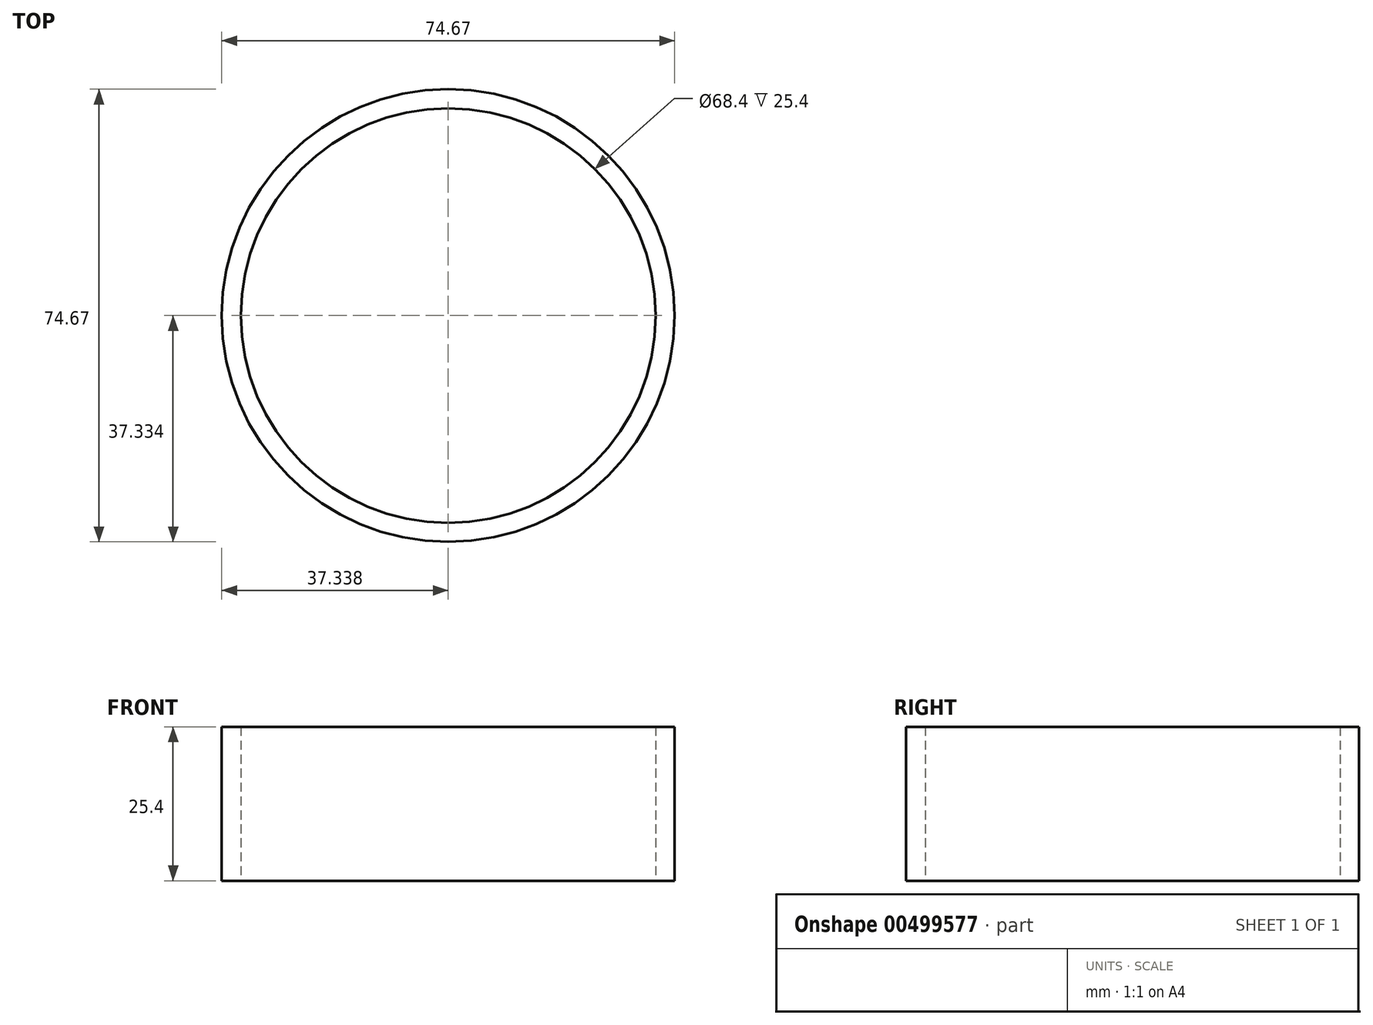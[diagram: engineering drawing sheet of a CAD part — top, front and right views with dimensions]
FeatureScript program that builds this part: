
annotation { "Feature Type Name" : "Feature", "Feature Type Description" : "" }
export const myFeature = defineFeature(function(context is Context, id is Id, definition is map)
    precondition{}
    {
        {
            var Q0;
            Q0=qCreatedBy(makeId("Top.planeOp"),FACE);
            var sketch = newSketch(context, id + "F0", { "sketchPlane" : qUnion([Q0])});
            skCircle(sketch, "E0", {"center": v(26.48, 36.26) * mm, "radius": 37.34 * mm});
            skCircle(sketch, "E1", {"center": v(26.48, 36.26) * mm, "radius": 34.2 * mm});
            skSolve(sketch);
        }
        {
            var Q0;
            Q0=qSketchRegion(id+"F0",true);
            extrude(context, id + "F1", {"entities" : qUnion([Q0]), "depth" : 25.4 * mm});
        }
    });
